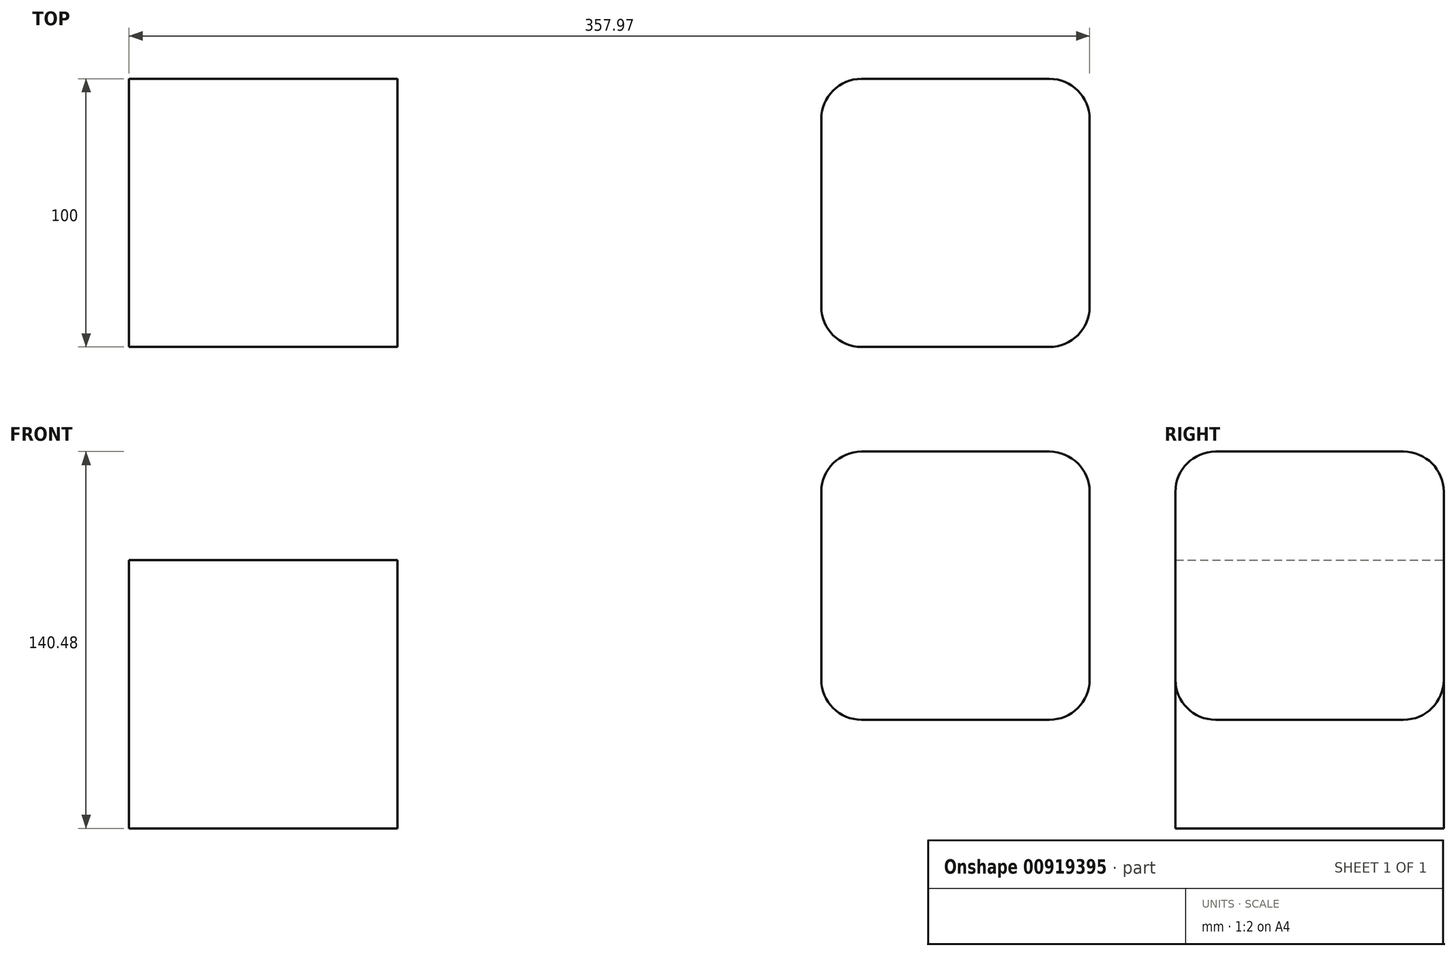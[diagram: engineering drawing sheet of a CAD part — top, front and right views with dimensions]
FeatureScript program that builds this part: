
annotation { "Feature Type Name" : "Feature", "Feature Type Description" : "" }
export const myFeature = defineFeature(function(context is Context, id is Id, definition is map)
    precondition{}
    {
        {
            var Q0;
            Q0=qCreatedBy(makeId("Front.planeOp"),FACE);
            var sketch = newSketch(context, id + "F0", { "sketchPlane" : qUnion([Q0])});
            skLineSegment(sketch, "E0.bottom", {"start": v(0, 0) * mm, "end": v(100, 0) * mm});
            skLineSegment(sketch, "E0.top", {"start": v(0, 100) * mm, "end": v(100, 100) * mm});
            skLineSegment(sketch, "E0.left", {"start": v(0, 0) * mm, "end": v(0, 100) * mm});
            skLineSegment(sketch, "E0.right", {"start": v(100, 0) * mm, "end": v(100, 100) * mm});
            skSolve(sketch);
        }
        {
            var Q0;
            Q0 = qSketchRegion(id + "F0", true);
            extrude(context, id + "F1", {"entities" : qUnion([Q0]), "depth" : 100 * mm, "offsetDistance" : 25 * mm});
        }
        {
            var Q0;
            Q0=makeQuery(id+"F1.opExtrude","SWEPT_FACE",FACE,{"disambiguationData":[OSD([sQuery(id+"F0.wireOp",EDGE,"E0.top")])]});
            var Q1;
            Q1=makeQuery(id+"F1.opExtrude","CAP_EDGE",EDGE,{"disambiguationData":[OSD([sQuery(id+"F0.wireOp",EDGE,"E0.right")])],"isStart":false});
            var Q2;
            Q2=makeQuery(id+"F1.opExtrude","CAP_EDGE",EDGE,{"disambiguationData":[OSD([sQuery(id+"F0.wireOp",EDGE,"E0.right")])],"isStart":true});
            var Q3;
            Q3=makeQuery(id+"F1.opExtrude","CAP_EDGE",EDGE,{"disambiguationData":[OSD([sQuery(id+"F0.wireOp",EDGE,"E0.left")])],"isStart":false});
            var Q4;
            Q4=makeQuery(id+"F1.opExtrude","CAP_EDGE",EDGE,{"disambiguationData":[OSD([sQuery(id+"F0.wireOp",EDGE,"E0.left")])],"isStart":true});
            var Q5;
            Q5=makeQuery(id+"F1.opExtrude","SWEPT_FACE",FACE,{"disambiguationData":[OSD([sQuery(id+"F0.wireOp",EDGE,"E0.bottom")])]});
            fillet(context, id + "F2", {"entities" : qUnion([Q0, Q1, Q2, Q3, Q4, Q5]), "radius" : 15 * mm, "tangentPropagation" : true, "allowEdgeOverflow" : false});
        }
        {
            var Q0;
            Q0=qCreatedBy(makeId("Front.planeOp"), FACE);
            var sketch = newSketch(context, id + "F3", { "sketchPlane" : qUnion([Q0])});
            skLineSegment(sketch, "E1.bottom", {"start": v(-257.97, 59.52) * mm, "end": v(-157.97, 59.52) * mm});
            skLineSegment(sketch, "E1.top", {"start": v(-257.97, -40.48) * mm, "end": v(-157.97, -40.48) * mm});
            skLineSegment(sketch, "E1.left", {"start": v(-257.97, 59.52) * mm, "end": v(-257.97, -40.48) * mm});
            skLineSegment(sketch, "E1.right", {"start": v(-157.97, 59.52) * mm, "end": v(-157.97, -40.48) * mm});
            skSolve(sketch);
        }
        {
            var Q0;
            Q0 = qSketchRegion(id + "F3", true);
            extrude(context, id + "F4", {"entities" : qUnion([Q0]), "depth" : 100 * mm, "offsetDistance" : 25 * mm});
        }
    });
